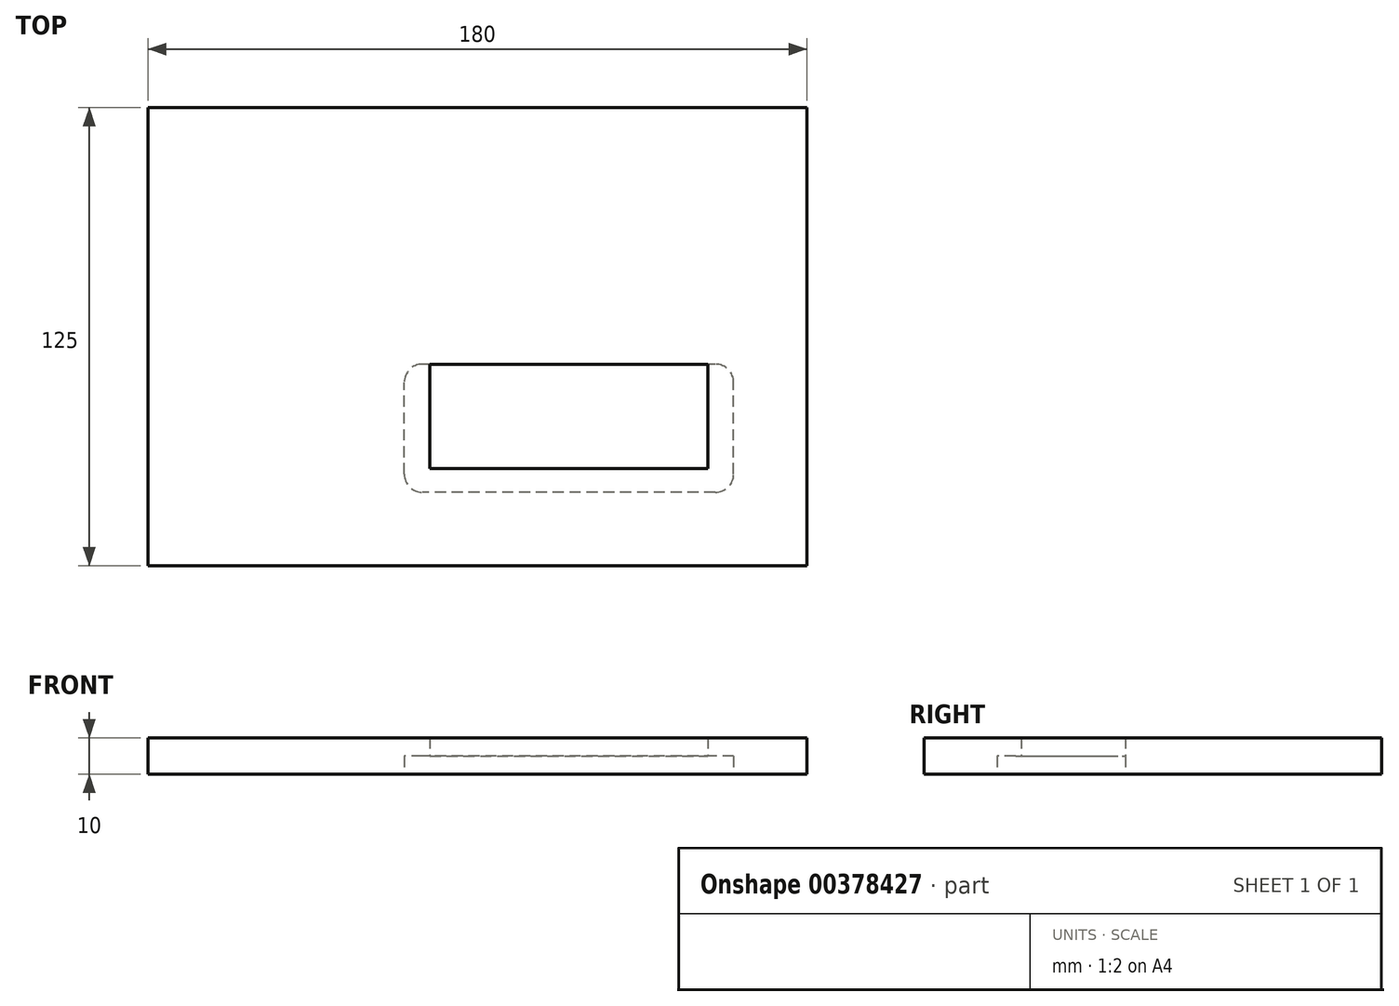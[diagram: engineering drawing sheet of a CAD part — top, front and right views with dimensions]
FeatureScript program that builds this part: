
annotation { "Feature Type Name" : "Feature", "Feature Type Description" : "" }
export const myFeature = defineFeature(function(context is Context, id is Id, definition is map)
    precondition{}
    {
        {
            var Q0;
            Q0=qCreatedBy(makeId("Top.planeOp"),FACE);
            var sketch = newSketch(context, id + "F0", { "sketchPlane" : qUnion([Q0])});
            skLineSegment(sketch, "E0", {"start": v(-90, 62.5) * mm, "end": v(90, 62.5) * mm});
            skLineSegment(sketch, "E1", {"start": v(90, 62.5) * mm, "end": v(90, -62.5) * mm});
            skLineSegment(sketch, "E2", {"start": v(90, -62.5) * mm, "end": v(-90, -62.5) * mm});
            skLineSegment(sketch, "E3", {"start": v(-90, -62.5) * mm, "end": v(-90, 62.5) * mm});
            skPoint(sketch, "E4.orphan", {"position": v(0, 62.5) * mm});
            skPoint(sketch, "E5.orphan", {"position": v(90, 0) * mm});
            skPoint(sketch, "E6.orphan", {"position": v(0, -62.5) * mm});
            skPoint(sketch, "E7.orphan", {"position": v(-90, 0) * mm});
            skSolve(sketch);
        }
        {
            var Q0;
            Q0=makeQuery(id+"F0.imprint","IMPRINT",FACE,{"disambiguationData":[TD([[makeQuery(id+"F0.imprint","IMPRINT",EDGE,{"derivedFrom":sQuery(id+"F0.wireOp",EDGE,"E0")}),-1.0]])]});
            extrude(context, id + "F1", {"entities" : qUnion([Q0]), "depth" : 10 * mm});
        }
        {
            var Q0;
            Q0=makeQuery(id+"F1.opExtrude","CAP_FACE",FACE,{"disambiguationData":[OSD([sQuery(id+"F0.wireOp",EDGE,"E0"),sQuery(id+"F0.wireOp",EDGE,"E1"),sQuery(id+"F0.wireOp",EDGE,"E2"),sQuery(id+"F0.wireOp",EDGE,"E3")])],"isStart":true});
            var sketch = newSketch(context, id + "F2", { "sketchPlane" : qUnion([Q0])});
            skLineSegment(sketch, "E8", {"start": v(70, 37.5) * mm, "end": v(70, 12.5) * mm});
            skLineSegment(sketch, "E9", {"start": v(65, 7.5) * mm, "end": v(-15, 7.5) * mm});
            skLineSegment(sketch, "E10", {"start": v(65, 42.5) * mm, "end": v(-15, 42.5) * mm});
            skLineSegment(sketch, "E11", {"start": v(-20, 37.5) * mm, "end": v(-20, 12.5) * mm});
            skPoint(sketch, "E12.visualSharp", {"position": v(70, 42.5) * mm});
            skArc(sketch, "E12.filletArc", {"start": v(70, 37.5) * mm, "mid": v(68.54, 41.04) * mm, "end": v(65, 42.5) * mm});
            skPoint(sketch, "E13.visualSharp", {"position": v(70, 7.5) * mm});
            skArc(sketch, "E13.filletArc", {"start": v(65, 7.5) * mm, "mid": v(68.54, 8.96) * mm, "end": v(70, 12.5) * mm});
            skPoint(sketch, "E14.visualSharp", {"position": v(-20, 42.5) * mm});
            skArc(sketch, "E14.filletArc", {"start": v(-15, 42.5) * mm, "mid": v(-18.54, 41.04) * mm, "end": v(-20, 37.5) * mm});
            skPoint(sketch, "E15.visualSharp", {"position": v(-20, 7.5) * mm});
            skArc(sketch, "E15.filletArc", {"start": v(-20, 12.5) * mm, "mid": v(-18.54, 8.96) * mm, "end": v(-15, 7.5) * mm});
            skSolve(sketch);
        }
        {
            var Q0;
            Q0=makeQuery(id+"F2.imprint","IMPRINT",FACE,{"disambiguationData":[TD([[makeQuery(id+"F2.imprint","IMPRINT",EDGE,{"derivedFrom":sQuery(id+"F2.wireOp",EDGE,"E8")}),-1.0]])]});
            extrude(context, id + "F3", {"entities" : qUnion([Q0]), "operationType" : NewBodyOperationType.REMOVE, "oppositeDirection" : true, "depth" : 5 * mm});
        }
        {
            var Q0;
            Q0=makeQuery(id+"F3.boolean.opBoolean","COPY",FACE,{"derivedFrom":makeQuery(id+"F3.opExtrude","CAP_FACE",FACE,{"disambiguationData":[OSD([sQuery(id+"F2.wireOp",EDGE,"E8"),sQuery(id+"F2.wireOp",EDGE,"E9"),sQuery(id+"F2.wireOp",EDGE,"E10"),sQuery(id+"F2.wireOp",EDGE,"E11"),sQuery(id+"F2.wireOp",EDGE,"E12.filletArc"),sQuery(id+"F2.wireOp",EDGE,"E13.filletArc"),sQuery(id+"F2.wireOp",EDGE,"E14.filletArc"),sQuery(id+"F2.wireOp",EDGE,"E15.filletArc")])],"isStart":false})});
            var sketch = newSketch(context, id + "F4", { "sketchPlane" : qUnion([Q0])});
            skLineSegment(sketch, "E16", {"start": v(-13, 36) * mm, "end": v(-13, 7.5) * mm});
            skLineSegment(sketch, "E17", {"start": v(63, 36) * mm, "end": v(63, 7.5) * mm});
            skLineSegment(sketch, "E18", {"start": v(-13, 42.5) * mm, "end": v(25, 42.5) * mm});
            skPoint(sketch, "E19.orphan", {"position": v(25, 42.5) * mm});
            skLineSegment(sketch, "E20.0", {"start": v(-13, 36) * mm, "end": v(63, 36) * mm});
            skLineSegment(sketch, "E21", {"start": v(63, 7.5) * mm, "end": v(-13, 7.5) * mm});
            skSolve(sketch);
        }
        {
            var Q0;
            Q0 = qSketchRegion(id + "F4", true);
            extrude(context, id + "F5", {"entities" : qUnion([Q0]), "operationType" : NewBodyOperationType.REMOVE, "endBound" : BoundingType.THROUGH_ALL, "oppositeDirection" : true, "depth" : 25 * mm});
        }
    });
